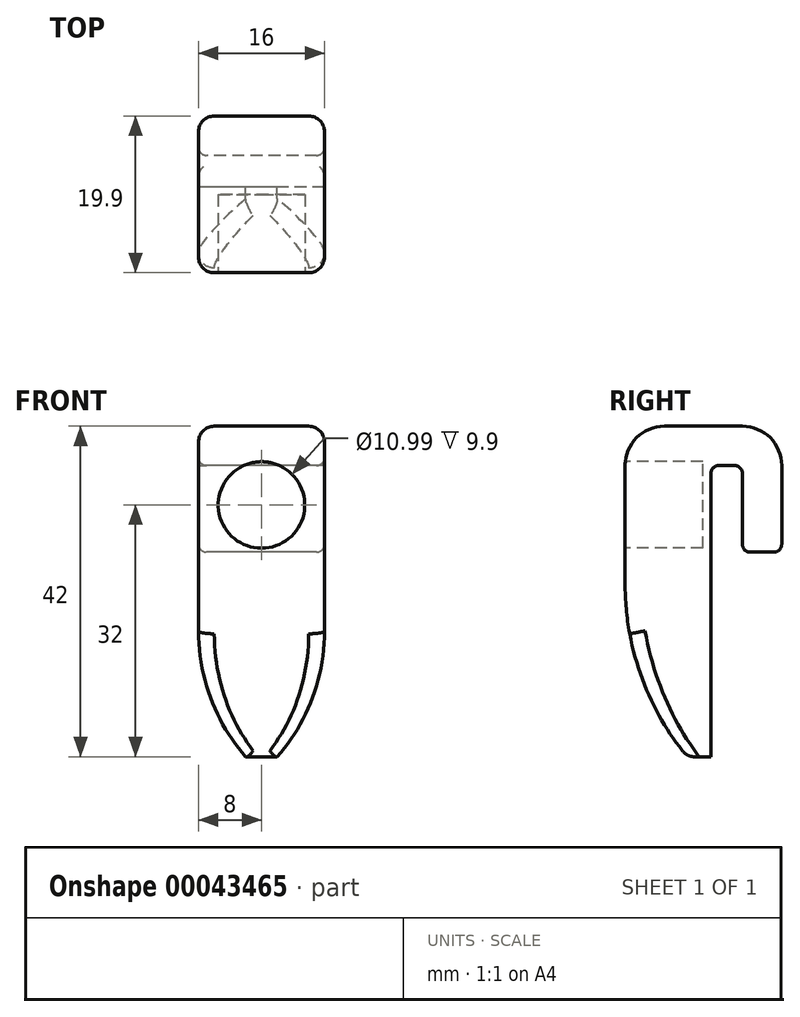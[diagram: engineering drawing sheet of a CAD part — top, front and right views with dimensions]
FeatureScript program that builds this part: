
annotation { "Feature Type Name" : "Feature", "Feature Type Description" : "" }
export const myFeature = defineFeature(function(context is Context, id is Id, definition is map)
    precondition{}
    {
        {
            var Q0;
            Q0=qCreatedBy(makeId("Right.planeOp"),FACE);
            var sketch = newSketch(context, id + "F0", { "sketchPlane" : qUnion([Q0])});
            skLineSegment(sketch, "E0", {"start": v(13.47, 26) * mm, "end": v(18.47, 26) * mm});
            skLineSegment(sketch, "E1", {"start": v(18.47, 26) * mm, "end": v(18.47, 42) * mm});
            skLineSegment(sketch, "E2", {"start": v(18.47, 42) * mm, "end": v(-1.43, 42) * mm});
            skLineSegment(sketch, "E3", {"start": v(-1.43, 42) * mm, "end": v(-1.43, 22) * mm});
            skLineSegment(sketch, "E4", {"start": v(13.47, 26) * mm, "end": v(13.47, 37) * mm});
            skLineSegment(sketch, "E5", {"start": v(13.47, 37) * mm, "end": v(9.47, 37) * mm});
            skLineSegment(sketch, "E6", {"start": v(9.47, 37) * mm, "end": v(9.47, 0) * mm});
            skLineSegment(sketch, "E7", {"start": v(9.47, 0) * mm, "end": v(6.47, 0) * mm});
            skArc(sketch, "E8", {"start": v(-1.43, 22) * mm, "mid": v(0.6, 10.31) * mm, "end": v(6.47, 0) * mm});
            skSolve(sketch);
        }
        {
            var Q0;
            Q0 = qSketchRegion(id + "F0", true);
            extrude(context, id + "F1", {"entities" : qUnion([Q0]), "endBound" : BoundingType.SYMMETRIC, "depth" : 16 * mm});
        }
        {
            var Q0;
            Q0=makeQuery(id+"F1.opExtrude","SWEPT_FACE",FACE,{"disambiguationData":[OSD([sQuery(id+"F0.wireOp",EDGE,"E6")])]});
            var sketch = newSketch(context, id + "F2", { "sketchPlane" : qUnion([Q0])});
            skArc(sketch, "E9", {"start": v(-8, 16) * mm, "mid": v(-6.45, 7.46) * mm, "end": v(-2, 0) * mm});
            skArc(sketch, "E10", {"start": v(2, 0) * mm, "mid": v(6.45, 7.46) * mm, "end": v(8, 16) * mm});
            skLineSegment(sketch, "E11", {"start": v(-8, 16) * mm, "end": v(-8, 0) * mm});
            skLineSegment(sketch, "E12", {"start": v(-8, 0) * mm, "end": v(-2, 0) * mm});
            skLineSegment(sketch, "E13", {"start": v(8, 16) * mm, "end": v(8, 0) * mm});
            skLineSegment(sketch, "E14", {"start": v(8, 0) * mm, "end": v(2, 0) * mm});
            skSolve(sketch);
        }
        {
            var Q0;
            Q0 = qSketchRegion(id + "F2", true);
            extrude(context, id + "F3", {"entities" : qUnion([Q0]), "operationType" : NewBodyOperationType.REMOVE, "endBound" : BoundingType.THROUGH_ALL, "oppositeDirection" : true, "depth" : 25 * mm});
        }
        {
            var Q0;
            Q0=makeQuery(id+"F1.opExtrude","SWEPT_FACE",FACE,{"disambiguationData":[OSD([sQuery(id+"F0.wireOp",EDGE,"E3")])]});
            var sketch = newSketch(context, id + "F4", { "sketchPlane" : qUnion([Q0])});
            skCircle(sketch, "E15", {"center": v(0, 32) * mm, "radius": 5.5 * mm});
            skPoint(sketch, "E16", {"position": v(8, 32) * mm});
            skSolve(sketch);
        }
        {
            var Q0;
            Q0 = qSketchRegion(id + "F4", true);
            extrude(context, id + "F5", {"entities" : qUnion([Q0]), "operationType" : NewBodyOperationType.REMOVE, "oppositeDirection" : true, "depth" : 9.9 * mm});
        }
        {
            var Q0;
            Q0=makeQuery(id+"F1.opExtrude","SWEPT_EDGE",EDGE,{"disambiguationData":[OSD([sQuery(id+"F0.wireOp",EDGE,"E2"),sQuery(id+"F0.wireOp",EDGE,"E3")])]});
            var Q1;
            Q1=makeQuery(id+"F1.opExtrude","SWEPT_EDGE",EDGE,{"disambiguationData":[OSD([sQuery(id+"F0.wireOp",EDGE,"E1"),sQuery(id+"F0.wireOp",EDGE,"E2")])]});
            fillet(context, id + "F6", {"entities" : qUnion([Q0, Q1]), "radius" : 5 * mm, "tangentPropagation" : true, "allowEdgeOverflow" : false});
        }
        {
            var Q0;
            Q0=makeQuery(id+"F1.opExtrude","CAP_EDGE",EDGE,{"disambiguationData":[OSD([sQuery(id+"F0.wireOp",EDGE,"E8")])],"isStart":true});
            var Q1;
            Q1=makeQuery(id+"F1.opExtrude","CAP_EDGE",EDGE,{"disambiguationData":[OSD([sQuery(id+"F0.wireOp",EDGE,"E8")])],"isStart":false});
            var Q2;
            Q2=makeQuery(id+"F3.boolean.opBoolean","COPY",EDGE,{"derivedFrom":makeQuery(id+"F3.opExtrude","SWEPT_EDGE",EDGE,{"disambiguationData":[OSD([sQuery(id+"F0.wireOp",EDGE,"E6"),sQuery(id+"F0.wireOp",EDGE,"E7"),sQuery(id+"F2.wireOp",EDGE,"E10"),sQuery(id+"F2.wireOp",EDGE,"E14")])]})});
            var Q3;
            Q3=makeQuery(id+"F3.boolean.opBoolean","COPY",EDGE,{"derivedFrom":makeQuery(id+"F3.opExtrude","SWEPT_EDGE",EDGE,{"disambiguationData":[OSD([sQuery(id+"F0.wireOp",EDGE,"E6"),sQuery(id+"F0.wireOp",EDGE,"E7"),sQuery(id+"F2.wireOp",EDGE,"E9"),sQuery(id+"F2.wireOp",EDGE,"E12")])]})});
            var Q4;
            Q4=makeQuery(id+"F1.opExtrude","SWEPT_EDGE",EDGE,{"disambiguationData":[OSD([sQuery(id+"F0.wireOp",EDGE,"E7"),sQuery(id+"F0.wireOp",EDGE,"E8")])]});
            fillet(context, id + "F7", {"entities" : qUnion([Q0, Q1, Q2, Q3, Q4]), "radius" : 2 * mm, "tangentPropagation" : true, "allowEdgeOverflow" : false});
        }
        {
            var Q0;
            Q0=makeQuery(id+"F1.opExtrude","SWEPT_EDGE",EDGE,{"disambiguationData":[OSD([sQuery(id+"F0.wireOp",EDGE,"E5"),sQuery(id+"F0.wireOp",EDGE,"E6")])]});
            var Q1;
            Q1=makeQuery(id+"F1.opExtrude","SWEPT_EDGE",EDGE,{"disambiguationData":[OSD([sQuery(id+"F0.wireOp",EDGE,"E4"),sQuery(id+"F0.wireOp",EDGE,"E5")])]});
            var Q2;
            Q2=makeQuery(id+"F1.opExtrude","SWEPT_EDGE",EDGE,{"disambiguationData":[OSD([sQuery(id+"F0.wireOp",EDGE,"E0"),sQuery(id+"F0.wireOp",EDGE,"E4")])]});
            var Q3;
            Q3=makeQuery(id+"F1.opExtrude","CAP_EDGE",EDGE,{"disambiguationData":[OSD([sQuery(id+"F0.wireOp",EDGE,"E0")])],"isStart":true});
            var Q4;
            Q4=makeQuery(id+"F1.opExtrude","CAP_EDGE",EDGE,{"disambiguationData":[OSD([sQuery(id+"F0.wireOp",EDGE,"E4")])],"isStart":true});
            var Q5;
            Q5=makeQuery(id+"F1.opExtrude","CAP_EDGE",EDGE,{"disambiguationData":[OSD([sQuery(id+"F0.wireOp",EDGE,"E4")])],"isStart":false});
            fillet(context, id + "F8", {"entities" : qUnion([Q0, Q1, Q2, Q3, Q4, Q5]), "radius" : 1 * mm, "tangentPropagation" : true, "allowEdgeOverflow" : false});
        }
    });
